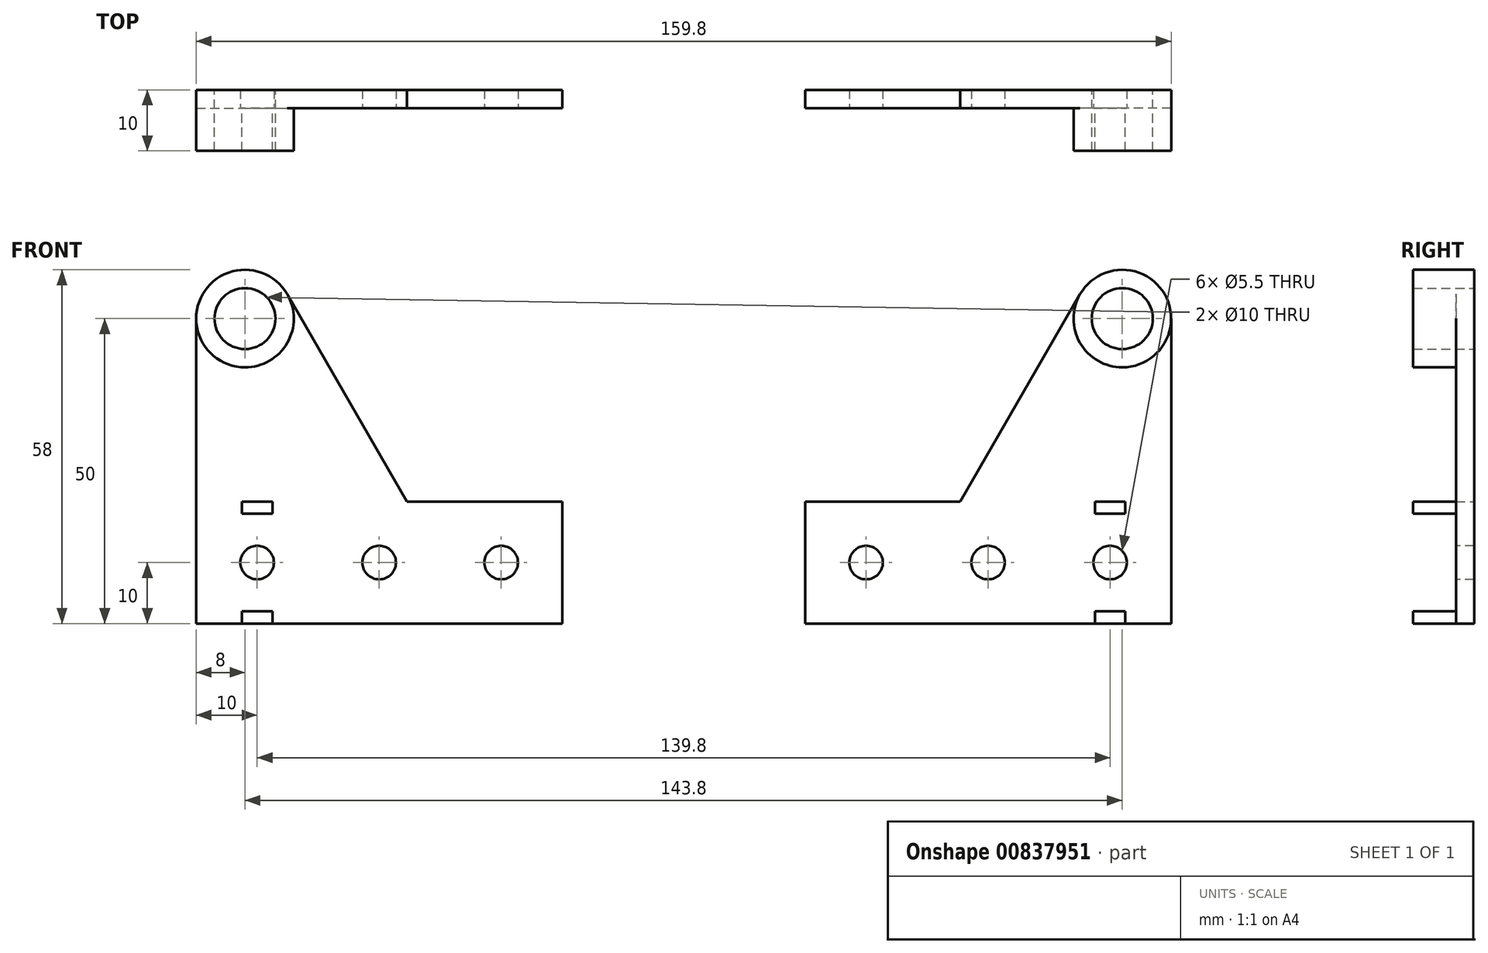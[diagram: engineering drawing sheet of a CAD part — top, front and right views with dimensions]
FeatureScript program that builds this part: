
annotation { "Feature Type Name" : "Feature", "Feature Type Description" : "" }
export const myFeature = defineFeature(function(context is Context, id is Id, definition is map)
    precondition{}
    {
        {
            var Q0;
            Q0=qCreatedBy(makeId("Front.planeOp"),FACE);
            var sketch = newSketch(context, id + "F0", { "sketchPlane" : qUnion([Q0])});
            skPoint(sketch, "E0", {"position": v(-20, 0) * mm});
            skLineSegment(sketch, "E1.bottom", {"start": v(-30, 10) * mm, "end": v(30, 10) * mm});
            skLineSegment(sketch, "E1.top", {"start": v(-30, -10) * mm, "end": v(30, -10) * mm});
            skLineSegment(sketch, "E1.left", {"start": v(-30, 10) * mm, "end": v(-30, -10) * mm});
            skLineSegment(sketch, "E1.right", {"start": v(30, 10) * mm, "end": v(30, -10) * mm});
            skLineSegment(sketch, "E2", {"start": v(-20, 0) * mm, "end": v(-20, 10) * mm, "construction": true});
            skLineSegment(sketch, "E3", {"start": v(-20, 0) * mm, "end": v(-30, 0) * mm, "construction": true});
            skPoint(sketch, "E4", {"position": v(20, 0) * mm});
            skLineSegment(sketch, "E5", {"start": v(-20, 0) * mm, "end": v(0, 0) * mm, "construction": true});
            skLineSegment(sketch, "E6.top", {"start": v(-22.5, 8) * mm, "end": v(-17.5, 8) * mm});
            skLineSegment(sketch, "E6.left", {"start": v(-22.5, 10) * mm, "end": v(-22.5, 8) * mm});
            skLineSegment(sketch, "E6.right", {"start": v(-17.5, 10) * mm, "end": v(-17.5, 8) * mm});
            skLineSegment(sketch, "E7.MirrorCS", {"start": v(-22.5, -8) * mm, "end": v(-17.5, -8) * mm});
            skLineSegment(sketch, "E8.MirrorCS", {"start": v(-17.5, -10) * mm, "end": v(-17.5, -8) * mm});
            skLineSegment(sketch, "E9.MirrorCS", {"start": v(-22.5, -10) * mm, "end": v(-22.5, -8) * mm});
            skCircle(sketch, "E10", {"center": v(-22, 40) * mm, "radius": 8 * mm});
            skLineSegment(sketch, "E11", {"start": v(-30, 10) * mm, "end": v(-30, 40) * mm});
            skLineSegment(sketch, "E12", {"start": v(-15.07, 44) * mm, "end": v(4.56, 10) * mm});
            skCircle(sketch, "E13", {"center": v(-22, 40) * mm, "radius": 5 * mm});
            skPoint(sketch, "E14", {"position": v(-22, 45.03) * mm});
            skSolve(sketch);
        }
        {
            var Q0;
            {var subQ3=sQuery(id+"F0.wireOp",EDGE,"E1.left");Q0=makeQuery(id+"F0.imprint","IMPRINT",FACE,{"disambiguationData":[TD([[makeQuery(id+"F0.imprint","IMPRINT",EDGE,{"derivedFrom":subQ3}),1.0]])]});}
            var Q1;
            {var subQ3=sQuery(id+"F0.wireOp",EDGE,"E11");Q1=makeQuery(id+"F0.imprint","IMPRINT",FACE,{"disambiguationData":[TD([[makeQuery(id+"F0.imprint","IMPRINT",EDGE,{"derivedFrom":subQ3}),-1.0]])]});}
            extrude(context, id + "F1", {"entities" : qUnion([Q0, Q1]), "depth" : 3 * mm, "offsetDistance" : 25 * mm});
        }
        {
            var Q0;
            Q0=makeQuery(id+"F0.imprint","IMPRINT",FACE,{"disambiguationData":[TD([[makeQuery(id+"F0.imprint","IMPRINT",EDGE,{"derivedFrom":sQuery(id+"F0.wireOp",EDGE,"E6.top")}),1.0]])]});
            var Q1;
            Q1=makeQuery(id+"F0.imprint","IMPRINT",FACE,{"disambiguationData":[TD([[makeQuery(id+"F0.imprint","IMPRINT",EDGE,{"derivedFrom":sQuery(id+"F0.wireOp",EDGE,"E7.MirrorCS")}),-1.0]])]});
            var Q2;
            Q2=makeQuery(id+"F0.imprint","IMPRINT",FACE,{"disambiguationData":[TD([[makeQuery(id+"F0.imprint","IMPRINT",EDGE,{"derivedFrom":sQuery(id+"F0.wireOp",EDGE,"E13")}),-1.0]])]});
            extrude(context, id + "F2", {"entities" : qUnion([Q0, Q1, Q2]), "operationType" : NewBodyOperationType.ADD, "depth" : 10 * mm, "offsetDistance" : 25 * mm});
        }
        {
            var Q0;
            Q0=sQuery(id+"F0.wireOp",VERTEX,"E0");
            var Q1;
            Q1=sQuery(id+"F0.wireOp",VERTEX,"E4");
            var Q2;
            Q2=sQuery(id+"F0.wireOp",VERTEX,"E5.end");
            var Q3;
            Q3=makeQuery(id+"F1.opExtrude","SWEPT_BODY",BODY,{"disambiguationData":[OSD([sQuery(id+"F0.wireOp",EDGE,"E1.bottom"),sQuery(id+"F0.wireOp",EDGE,"E1.top"),sQuery(id+"F0.wireOp",EDGE,"E1.left"),sQuery(id+"F0.wireOp",EDGE,"E1.right"),sQuery(id+"F0.wireOp",EDGE,"E6.top"),sQuery(id+"F0.wireOp",EDGE,"E6.left"),sQuery(id+"F0.wireOp",EDGE,"E6.right"),sQuery(id+"F0.wireOp",EDGE,"E7.MirrorCS"),sQuery(id+"F0.wireOp",EDGE,"E8.MirrorCS"),sQuery(id+"F0.wireOp",EDGE,"E9.MirrorCS"),sQuery(id+"F0.wireOp",EDGE,"E10"),sQuery(id+"F0.wireOp",EDGE,"E11"),sQuery(id+"F0.wireOp",EDGE,"E12")])]});
            hole(context, id + "F3", {"style" : HoleStyle.SIMPLE, "endStyle" : HoleEndStyle.THROUGH, "oppositeDirection" : true, "standardTappedOrClearance" : lookupTablePath({ "fit" : "Normal", "standard" : "ISO", "size" : "M5", "type" : "Clearance" }), "standardBlindInLast" : lookupTablePath({ "fit" : "Standard", "standard" : "ISO", "size" : "M5", "type" : "Clearance" }), "holeDiameter" : 5.5 * mm, "majorDiameter" : 5 * mm, "isTappedThrough" : true, "tappedDepth" : 12 * mm, "tapClearance" : 3, "startFromSketch" : true, "locations" : qUnion([Q0, Q1, Q2]), "scope" : qUnion([Q3])});
        }
        {
            var Q0;
            Q0=qCreatedBy(makeId("Right.planeOp"),FACE);
            cPlane(context, id + "F4", {"entities" : qUnion([Q0]), "cplaneType" : CPlaneType.OFFSET, "offset" : 49.9 * mm, "width" : 150 * mm, "height" : 150 * mm});
        }
        {
            var Q0;
            Q0=makeQuery(id+"F1.opExtrude","SWEPT_BODY",BODY,{"disambiguationData":[OSD([sQuery(id+"F0.wireOp",EDGE,"E1.bottom"),sQuery(id+"F0.wireOp",EDGE,"E1.top"),sQuery(id+"F0.wireOp",EDGE,"E1.left"),sQuery(id+"F0.wireOp",EDGE,"E1.right"),sQuery(id+"F0.wireOp",EDGE,"E6.top"),sQuery(id+"F0.wireOp",EDGE,"E6.left"),sQuery(id+"F0.wireOp",EDGE,"E6.right"),sQuery(id+"F0.wireOp",EDGE,"E7.MirrorCS"),sQuery(id+"F0.wireOp",EDGE,"E8.MirrorCS"),sQuery(id+"F0.wireOp",EDGE,"E9.MirrorCS"),sQuery(id+"F0.wireOp",EDGE,"E10"),sQuery(id+"F0.wireOp",EDGE,"E11"),sQuery(id+"F0.wireOp",EDGE,"E12")])]});
            var Q1;
            Q1=qCreatedBy(id+"F4.planeOp",FACE);
            mirror(context, id + "F5", {"entities" : qUnion([Q0]), "mirrorPlane" : qUnion([Q1])});
        }
    });
